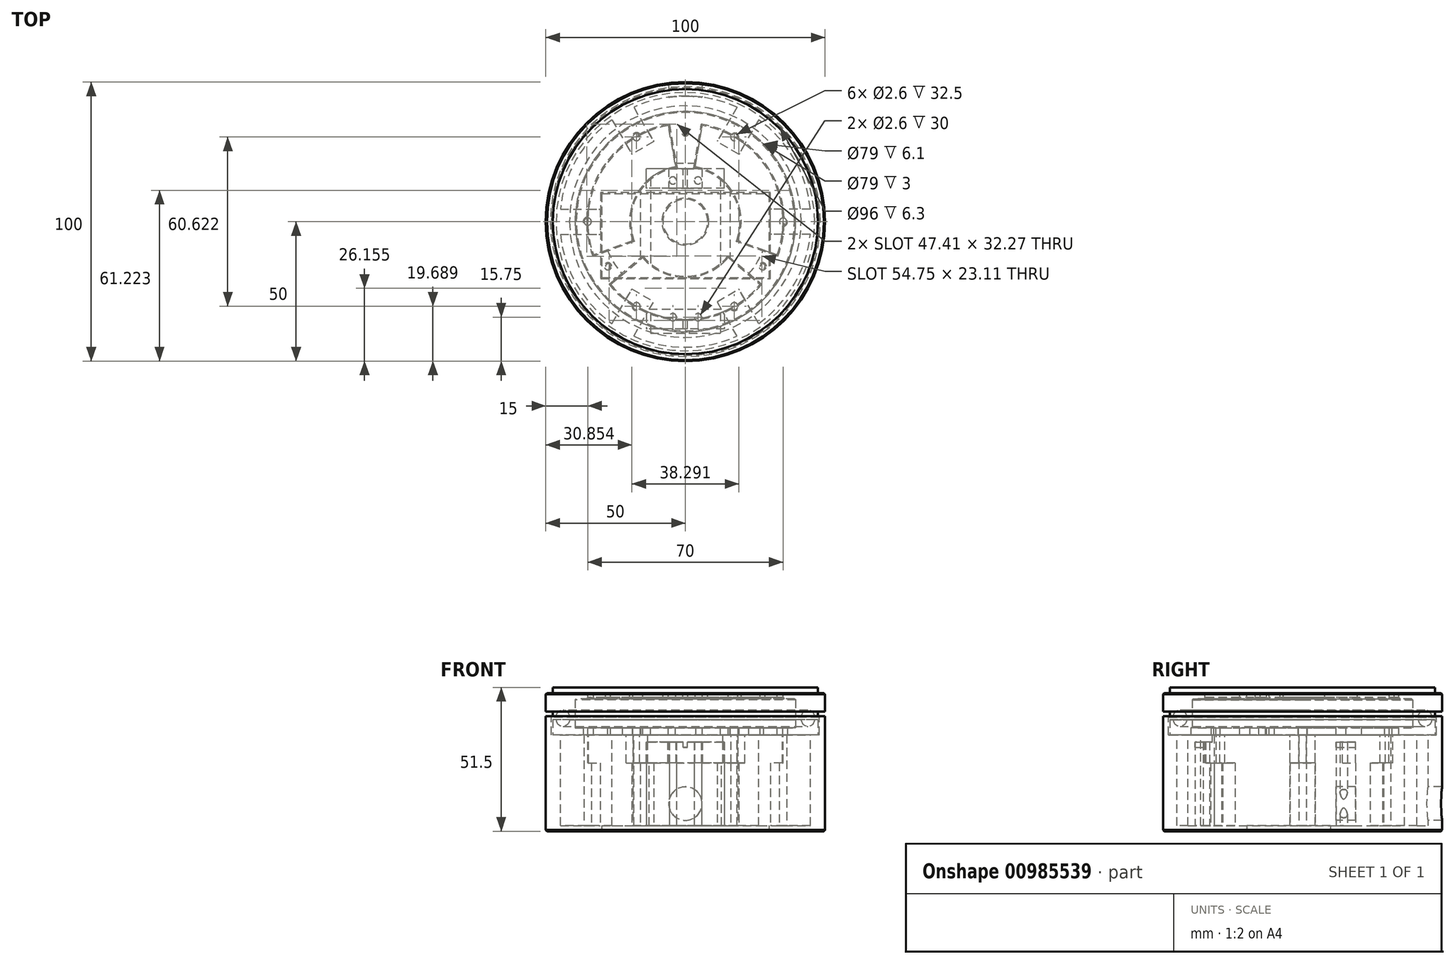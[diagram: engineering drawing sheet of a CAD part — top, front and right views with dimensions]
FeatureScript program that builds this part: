
annotation { "Feature Type Name" : "Feature", "Feature Type Description" : "" }
export const myFeature = defineFeature(function(context is Context, id is Id, definition is map)
    precondition{}
    {
        {
            var Q0;
            Q0=qCreatedBy(makeId("Top.planeOp"),FACE);
            var sketch = newSketch(context, id + "F0", { "sketchPlane" : qUnion([Q0])});
            skCircle(sketch, "E0", {"center": v(0, 0) * mm, "radius": 50 * mm});
            skLineSegment(sketch, "E1.bottom", {"start": v(-30, 10) * mm, "end": v(30, 10) * mm});
            skLineSegment(sketch, "E1.top", {"start": v(-30, -20) * mm, "end": v(30, -20) * mm});
            skLineSegment(sketch, "E1.left", {"start": v(-30, 10) * mm, "end": v(-30, -20) * mm});
            skLineSegment(sketch, "E1.right", {"start": v(30, 10) * mm, "end": v(30, -20) * mm});
            skPoint(sketch, "E2", {"position": v(0, 10) * mm});
            skSolve(sketch);
        }
        {
            var Q0;
            Q0=qSketchRegion(id+"F0",true);
            extrude(context, id + "F1", {"entities" : qUnion([Q0]), "depth" : 2 * mm, "offsetDistance" : 25 * mm});
        }
        {
            var Q0;
            Q0=qCreatedBy(makeId("Front.planeOp"),FACE);
            var sketch = newSketch(context, id + "F2", { "sketchPlane" : qUnion([Q0])});
            skLineSegment(sketch, "E3", {"start": v(45, 2) * mm, "end": v(50, 2) * mm});
            skLineSegment(sketch, "E4", {"start": v(50, 2) * mm, "end": v(50, 41.2) * mm});
            skLineSegment(sketch, "E5", {"start": v(50, 41.2) * mm, "end": v(48, 41.2) * mm});
            skLineSegment(sketch, "E6", {"start": v(48, 41.2) * mm, "end": v(48, 34.5) * mm});
            skLineSegment(sketch, "E7", {"start": v(48, 34.5) * mm, "end": v(45, 34.5) * mm});
            skLineSegment(sketch, "E8", {"start": v(45, 34.5) * mm, "end": v(45, 2) * mm});
            skSolve(sketch);
        }
        {
            var Q0;
            Q0 = qSketchRegion(id + "F2", true);
            var Q1;
            Q1=makeQuery(id+"F1.opExtrude","CAP_EDGE",EDGE,{"disambiguationData":[OSD([sQuery(id+"F0.wireOp",EDGE,"E0")])],"isStart":false});
            sweep(context, id + "F3", {"operationType" : NewBodyOperationType.ADD, "profiles" : qUnion([Q0]), "path" : qUnion([Q1])});
        }
        {
            var Q0;
            {var subQ0=sQuery(id+"F0.wireOp",EDGE,"E0");var subQ1=sQuery(id+"F0.wireOp",EDGE,"wwXRvqXR-i3DQ-b2GX-zRsi-UhwsgNiWwsgo");Q0=makeQuery(id+"F7.boolean.opBoolean","SPLIT",FACE,{"disambiguationData":[TD([makeQuery(id+"F1.opExtrude","SWEPT_FACE",FACE,{"disambiguationData":[OSD([subQ1])]})])],"derivedFrom":makeQuery(id+"F1.opExtrude","CAP_FACE",FACE,{"disambiguationData":[OSD([subQ1,subQ0])],"isStart":false})});}
            var sketch = newSketch(context, id + "F4", { "sketchPlane" : qUnion([Q0])});
            skLineSegment(sketch, "E9.bottom", {"start": v(45.5, -4.5) * mm, "end": v(30.5, -4.5) * mm});
            skLineSegment(sketch, "E9.top", {"start": v(45.5, 4.5) * mm, "end": v(30.5, 4.5) * mm});
            skLineSegment(sketch, "E9.left", {"start": v(45.5, -4.5) * mm, "end": v(45.5, 4.5) * mm});
            skLineSegment(sketch, "E9.right", {"start": v(30.5, -4.5) * mm, "end": v(30.5, 4.5) * mm});
            skPoint(sketch, "E9.middle", {"position": v(38, 0) * mm});
            skCircle(sketch, "E10", {"center": v(35, 0) * mm, "radius": 1.3 * mm});
            skLineSegment(sketch, "E11.1.0", {"start": v(19.15, 24.16) * mm, "end": v(11.35, 28.66) * mm});
            skLineSegment(sketch, "E11.1.1", {"start": v(18.85, 41.65) * mm, "end": v(11.35, 28.66) * mm});
            skCircle(sketch, "E11.1.2", {"center": v(17.5, 30.31) * mm, "radius": 1.3 * mm});
            skLineSegment(sketch, "E11.1.3", {"start": v(26.65, 37.15) * mm, "end": v(18.85, 41.65) * mm});
            skPoint(sketch, "E11.1.4", {"position": v(19, 32.9) * mm});
            skLineSegment(sketch, "E11.1.5", {"start": v(26.65, 37.15) * mm, "end": v(19.15, 24.16) * mm});
            skLineSegment(sketch, "E11.2.0", {"start": v(-11.35, 28.66) * mm, "end": v(-19.15, 24.16) * mm});
            skLineSegment(sketch, "E11.2.1", {"start": v(-26.65, 37.15) * mm, "end": v(-19.15, 24.16) * mm});
            skCircle(sketch, "E11.2.2", {"center": v(-17.5, 30.31) * mm, "radius": 1.3 * mm});
            skLineSegment(sketch, "E11.2.3", {"start": v(-18.85, 41.65) * mm, "end": v(-26.65, 37.15) * mm});
            skPoint(sketch, "E11.2.4", {"position": v(-19, 32.9) * mm});
            skLineSegment(sketch, "E11.2.5", {"start": v(-18.85, 41.65) * mm, "end": v(-11.35, 28.66) * mm});
            skLineSegment(sketch, "E11.3.0", {"start": v(-30.5, 4.5) * mm, "end": v(-30.5, -4.5) * mm});
            skLineSegment(sketch, "E11.3.1", {"start": v(-45.5, -4.5) * mm, "end": v(-30.5, -4.5) * mm});
            skCircle(sketch, "E11.3.2", {"center": v(-35, 0) * mm, "radius": 1.3 * mm});
            skLineSegment(sketch, "E11.3.3", {"start": v(-45.5, 4.5) * mm, "end": v(-45.5, -4.5) * mm});
            skPoint(sketch, "E11.3.4", {"position": v(-38, 0) * mm});
            skLineSegment(sketch, "E11.3.5", {"start": v(-45.5, 4.5) * mm, "end": v(-30.5, 4.5) * mm});
            skLineSegment(sketch, "E11.4.0", {"start": v(-19.15, -24.16) * mm, "end": v(-11.35, -28.66) * mm});
            skLineSegment(sketch, "E11.4.1", {"start": v(-18.85, -41.65) * mm, "end": v(-11.35, -28.66) * mm});
            skCircle(sketch, "E11.4.2", {"center": v(-17.5, -30.31) * mm, "radius": 1.3 * mm});
            skLineSegment(sketch, "E11.4.3", {"start": v(-26.65, -37.15) * mm, "end": v(-18.85, -41.65) * mm});
            skPoint(sketch, "E11.4.4", {"position": v(-19, -32.9) * mm});
            skLineSegment(sketch, "E11.4.5", {"start": v(-26.65, -37.15) * mm, "end": v(-19.15, -24.16) * mm});
            skLineSegment(sketch, "E11.5.0", {"start": v(11.35, -28.66) * mm, "end": v(19.15, -24.16) * mm});
            skLineSegment(sketch, "E11.5.1", {"start": v(26.65, -37.15) * mm, "end": v(19.15, -24.16) * mm});
            skCircle(sketch, "E11.5.2", {"center": v(17.5, -30.31) * mm, "radius": 1.3 * mm});
            skLineSegment(sketch, "E11.5.3", {"start": v(18.85, -41.65) * mm, "end": v(26.65, -37.15) * mm});
            skPoint(sketch, "E11.5.4", {"position": v(19, -32.9) * mm});
            skLineSegment(sketch, "E11.5.5", {"start": v(18.85, -41.65) * mm, "end": v(11.35, -28.66) * mm});
            skPoint(sketch, "E11.center", {"position": v(0, 0) * mm});
            skSolve(sketch);
        }
        {
            var Q0;
            Q0 = qSketchRegion(id + "F4", true);
            var Q1;
            Q1=makeQuery(id+"F3.opSweep","SWEPT_FACE",FACE,{"disambiguationData":[OSD([sQuery(id+"F0.wireOp",EDGE,"E0"),sQuery(id+"F2.wireOp",EDGE,"E7")])]});
            extrude(context, id + "F5", {"entities" : qUnion([Q0]), "operationType" : NewBodyOperationType.ADD, "endBound" : BoundingType.UP_TO_SURFACE, "depth" : 25 * mm, "endBoundEntityFace" : qUnion([Q1]), "offsetDistance" : 25 * mm});
        }
        {
            var Q0;
            Q0=makeQuery(id+"F1.opExtrude","CAP_FACE",FACE,{"disambiguationData":[OSD([sQuery(id+"F0.wireOp",EDGE,"wwXRvqXR-i3DQ-b2GX-zRsi-UhwsgNiWwsgo"),sQuery(id+"F0.wireOp",EDGE,"E0")])],"isStart":false});
            var sketch = newSketch(context, id + "F6", { "sketchPlane" : qUnion([Q0])});
            skLineSegment(sketch, "E12", {"start": v(0, 0) * mm, "end": v(0, 4.6) * mm});
            skCircle(sketch, "E13", {"center": v(-4.5, 14.75) * mm, "radius": 1.3 * mm});
            skLineSegment(sketch, "E14.bottom", {"start": v(14, 12) * mm, "end": v(-14, 12) * mm});
            skLineSegment(sketch, "E14.top", {"start": v(14, 19) * mm, "end": v(-14, 19) * mm});
            skLineSegment(sketch, "E14.left", {"start": v(14, 12) * mm, "end": v(14, 19) * mm});
            skLineSegment(sketch, "E14.right", {"start": v(-14, 12) * mm, "end": v(-14, 19) * mm});
            skPoint(sketch, "E14.middle", {"position": v(0, 15.5) * mm});
            skCircle(sketch, "E15.MirrorC", {"center": v(4.5, 14.75) * mm, "radius": 1.3 * mm});
            skLineSegment(sketch, "E16", {"start": v(13.6, -9.75) * mm, "end": v(-3, -9.75) * mm});
            skPoint(sketch, "E17.MirrorP", {"position": v(0, -35) * mm});
            skLineSegment(sketch, "E18.MirrorCS", {"start": v(-14, -31.5) * mm, "end": v(-14, -38.5) * mm});
            skLineSegment(sketch, "E19.MirrorCS", {"start": v(14, -38.5) * mm, "end": v(-14, -38.5) * mm});
            skLineSegment(sketch, "E20.MirrorCS", {"start": v(14, -31.5) * mm, "end": v(-14, -31.5) * mm});
            skCircle(sketch, "E21.MirrorC", {"center": v(4.5, -34.25) * mm, "radius": 1.3 * mm});
            skLineSegment(sketch, "E22.MirrorCS", {"start": v(14, -31.5) * mm, "end": v(14, -38.5) * mm});
            skCircle(sketch, "E23.MirrorC", {"center": v(-4.5, -34.25) * mm, "radius": 1.3 * mm});
            skSolve(sketch);
        }
        {
            var Q0;
            Q0=qSketchRegion(id+"F6",true);
            extrude(context, id + "F7", {"entities" : qUnion([Q0]), "operationType" : NewBodyOperationType.ADD, "depth" : 30 * mm, "offsetDistance" : 25 * mm});
        }
        {
            var Q0;
            Q0=qCreatedBy(makeId("Front.planeOp"),FACE);
            var sketch = newSketch(context, id + "F8", { "sketchPlane" : qUnion([Q0])});
            skCircle(sketch, "E24", {"center": v(0, 9.9) * mm, "radius": 6 * mm});
            skSolve(sketch);
        }
        {
            var Q0;
            Q0 = qSketchRegion(id + "F8", true);
            extrude(context, id + "F9", {"entities" : qUnion([Q0]), "operationType" : NewBodyOperationType.REMOVE, "oppositeDirection" : true, "depth" : 100 * mm, "offsetDistance" : 25 * mm});
        }
        {
            var Q0;
            Q0=makeQuery(id+"F7.opExtrude","CAP_FACE",FACE,{"disambiguationData":[OSD([sQuery(id+"F6.wireOp",EDGE,"E18.MirrorCS"),sQuery(id+"F6.wireOp",EDGE,"E19.MirrorCS"),sQuery(id+"F6.wireOp",EDGE,"E20.MirrorCS"),sQuery(id+"F6.wireOp",EDGE,"E21.MirrorC"),sQuery(id+"F6.wireOp",EDGE,"E22.MirrorCS"),sQuery(id+"F6.wireOp",EDGE,"E23.MirrorC")])],"isStart":false});
            var sketch = newSketch(context, id + "F10", { "sketchPlane" : qUnion([Q0])});
            skLineSegment(sketch, "E25.bottom", {"start": v(0.75, -39.15) * mm, "end": v(-0.75, -39.15) * mm});
            skLineSegment(sketch, "E25.top", {"start": v(0.75, 20.85) * mm, "end": v(-0.75, 20.85) * mm});
            skLineSegment(sketch, "E25.left", {"start": v(0.75, -39.15) * mm, "end": v(0.75, 20.85) * mm});
            skLineSegment(sketch, "E25.right", {"start": v(-0.75, -39.15) * mm, "end": v(-0.75, 20.85) * mm});
            skPoint(sketch, "E25.middle", {"position": v(0, -9.15) * mm});
            skPoint(sketch, "E25.middle.positionSnap0", {"position": v(0, -31.5) * mm});
            skPoint(sketch, "E25.centerSnap0", {"position": v(0, -31.5) * mm});
            skSolve(sketch);
        }
        {
            var Q0;
            Q0=qSketchRegion(id+"F10",true);
            extrude(context, id + "F11", {"entities" : qUnion([Q0]), "operationType" : NewBodyOperationType.REMOVE, "oppositeDirection" : true, "depth" : 2 * mm, "offsetDistance" : 25 * mm});
        }
        {
            var Q0;
            Q0=makeQuery(id+"F5.boolean.opBoolean","MERGE",FACE,{"derivedFrom":[makeQuery(id+"F3.opSweep","SWEPT_FACE",FACE,{"disambiguationData":[OSD([sQuery(id+"F0.wireOp",EDGE,"E0"),sQuery(id+"F2.wireOp",EDGE,"E7")])]}),makeQuery(id+"F5.opExtrude","CAP_FACE",FACE,{"disambiguationData":[OSD([sQuery(id+"F4.wireOp",EDGE,"Q81txGdN-tRcn-shot-oBIU-nrsWAsqUdM4r.bottom"),sQuery(id+"F4.wireOp",EDGE,"Q81txGdN-tRcn-shot-oBIU-nrsWAsqUdM4r.top"),sQuery(id+"F4.wireOp",EDGE,"Q81txGdN-tRcn-shot-oBIU-nrsWAsqUdM4r.left"),sQuery(id+"F4.wireOp",EDGE,"Q81txGdN-tRcn-shot-oBIU-nrsWAsqUdM4r.right"),sQuery(id+"F4.wireOp",EDGE,"7Wr9KYCT-SgnQ-EfTt-MQro-Hq332cc40vgq")])],"isStart":false}),makeQuery(id+"F5.opExtrude","CAP_FACE",FACE,{"disambiguationData":[OSD([sQuery(id+"F4.wireOp",EDGE,"5effae5a-cc89-4e3e-84d3-61618aa6fbcc.1.0"),sQuery(id+"F4.wireOp",EDGE,"5effae5a-cc89-4e3e-84d3-61618aa6fbcc.1.1"),sQuery(id+"F4.wireOp",EDGE,"5effae5a-cc89-4e3e-84d3-61618aa6fbcc.1.2"),sQuery(id+"F4.wireOp",EDGE,"5effae5a-cc89-4e3e-84d3-61618aa6fbcc.1.3"),sQuery(id+"F4.wireOp",EDGE,"5effae5a-cc89-4e3e-84d3-61618aa6fbcc.1.4")])],"isStart":false}),makeQuery(id+"F5.opExtrude","CAP_FACE",FACE,{"disambiguationData":[OSD([sQuery(id+"F4.wireOp",EDGE,"5effae5a-cc89-4e3e-84d3-61618aa6fbcc.2.0"),sQuery(id+"F4.wireOp",EDGE,"5effae5a-cc89-4e3e-84d3-61618aa6fbcc.2.1"),sQuery(id+"F4.wireOp",EDGE,"5effae5a-cc89-4e3e-84d3-61618aa6fbcc.2.2"),sQuery(id+"F4.wireOp",EDGE,"5effae5a-cc89-4e3e-84d3-61618aa6fbcc.2.3"),sQuery(id+"F4.wireOp",EDGE,"5effae5a-cc89-4e3e-84d3-61618aa6fbcc.2.4")])],"isStart":false}),makeQuery(id+"F5.opExtrude","CAP_FACE",FACE,{"disambiguationData":[OSD([sQuery(id+"F4.wireOp",EDGE,"5effae5a-cc89-4e3e-84d3-61618aa6fbcc.3.0"),sQuery(id+"F4.wireOp",EDGE,"5effae5a-cc89-4e3e-84d3-61618aa6fbcc.3.1"),sQuery(id+"F4.wireOp",EDGE,"5effae5a-cc89-4e3e-84d3-61618aa6fbcc.3.2"),sQuery(id+"F4.wireOp",EDGE,"5effae5a-cc89-4e3e-84d3-61618aa6fbcc.3.3"),sQuery(id+"F4.wireOp",EDGE,"5effae5a-cc89-4e3e-84d3-61618aa6fbcc.3.4")])],"isStart":false}),makeQuery(id+"F5.opExtrude","CAP_FACE",FACE,{"disambiguationData":[OSD([sQuery(id+"F4.wireOp",EDGE,"5c545cf2-7ed1-48a6-9170-971ede2a80a5.2.4.0"),sQuery(id+"F4.wireOp",EDGE,"5c545cf2-7ed1-48a6-9170-971ede2a80a5.3.4.0"),sQuery(id+"F4.wireOp",EDGE,"5c545cf2-7ed1-48a6-9170-971ede2a80a5.5.4.0"),sQuery(id+"F4.wireOp",EDGE,"5c545cf2-7ed1-48a6-9170-971ede2a80a5.8.4.0"),sQuery(id+"F4.wireOp",EDGE,"5c545cf2-7ed1-48a6-9170-971ede2a80a5.11.4.0")])],"isStart":false}),makeQuery(id+"F5.opExtrude","CAP_FACE",FACE,{"disambiguationData":[OSD([sQuery(id+"F4.wireOp",EDGE,"5c545cf2-7ed1-48a6-9170-971ede2a80a5.2.5.0"),sQuery(id+"F4.wireOp",EDGE,"5c545cf2-7ed1-48a6-9170-971ede2a80a5.3.5.0"),sQuery(id+"F4.wireOp",EDGE,"5c545cf2-7ed1-48a6-9170-971ede2a80a5.5.5.0"),sQuery(id+"F4.wireOp",EDGE,"5c545cf2-7ed1-48a6-9170-971ede2a80a5.8.5.0"),sQuery(id+"F4.wireOp",EDGE,"5c545cf2-7ed1-48a6-9170-971ede2a80a5.11.5.0")])],"isStart":false})]});
            var sketch = newSketch(context, id + "F12", { "sketchPlane" : qUnion([Q0])});
            skCircle(sketch, "E26", {"center": v(0, 0) * mm, "radius": 47.5 * mm});
            skCircle(sketch, "E27", {"center": v(35, 0) * mm, "radius": 1.6 * mm});
            skCircle(sketch, "E28.1.0", {"center": v(17.5, 30.31) * mm, "radius": 1.6 * mm});
            skCircle(sketch, "E28.2.0", {"center": v(-17.5, 30.31) * mm, "radius": 1.6 * mm});
            skCircle(sketch, "E28.3.0", {"center": v(-35, 0) * mm, "radius": 1.6 * mm});
            skCircle(sketch, "E28.4.0", {"center": v(-17.5, -30.31) * mm, "radius": 1.6 * mm});
            skCircle(sketch, "E28.5.0", {"center": v(17.5, -30.31) * mm, "radius": 1.6 * mm});
            skLineSegment(sketch, "E29.bottom", {"start": v(-12.5, 21) * mm, "end": v(12.5, 21) * mm});
            skLineSegment(sketch, "E29.top", {"start": v(-12.5, -40) * mm, "end": v(12.5, -40) * mm});
            skLineSegment(sketch, "E29.left", {"start": v(-12.5, 21) * mm, "end": v(-12.5, -40) * mm});
            skLineSegment(sketch, "E29.right", {"start": v(12.5, 21) * mm, "end": v(12.5, -40) * mm});
            skLineSegment(sketch, "E30", {"start": v(16, 0) * mm, "end": v(16, 24.61) * mm});
            skLineSegment(sketch, "E31", {"start": v(16, 0) * mm, "end": v(30, 0) * mm});
            skArc(sketch, "E32", {"start": v(30, 0) * mm, "mid": v(26.05, 14.04) * mm, "end": v(16, 24.61) * mm});
            skLineSegment(sketch, "E33.MirrorCS", {"start": v(16, 0) * mm, "end": v(16, -24.61) * mm});
            skArc(sketch, "E34.MirrorCS", {"start": v(30, 0) * mm, "mid": v(26.05, -14.04) * mm, "end": v(16, -24.61) * mm});
            skArc(sketch, "E35.MirrorCS", {"start": v(-30, 0) * mm, "mid": v(-26.05, 14.04) * mm, "end": v(-16, 24.61) * mm});
            skLineSegment(sketch, "E36.MirrorCS", {"start": v(-16, 0) * mm, "end": v(-30, 0) * mm});
            skArc(sketch, "E37.MirrorCS", {"start": v(-30, 0) * mm, "mid": v(-26.05, -14.04) * mm, "end": v(-16, -24.61) * mm});
            skLineSegment(sketch, "E38.MirrorCS", {"start": v(-16, 0) * mm, "end": v(-16, 24.61) * mm});
            skLineSegment(sketch, "E39.MirrorCS", {"start": v(-16, 0) * mm, "end": v(-16, -24.61) * mm});
            skSolve(sketch);
        }
        {
            var Q0;
            Q0 = qSketchRegion(id + "F12", true);
            extrude(context, id + "F13", {"entities" : qUnion([Q0]), "depth" : 2.5 * mm, "offsetDistance" : 25 * mm});
        }
        {
            var Q0;
            Q0=makeQuery(id+"F13.opExtrude","CAP_FACE",FACE,{"disambiguationData":[OSD([sQuery(id+"F12.wireOp",EDGE,"E26"),sQuery(id+"F12.wireOp",EDGE,"QdyFas2a-h3oe-I2XU-WaBX-7dCjf6wj1iEE"),sQuery(id+"F12.wireOp",EDGE,"E27"),sQuery(id+"F12.wireOp",EDGE,"E28.1.0"),sQuery(id+"F12.wireOp",EDGE,"E28.2.0"),sQuery(id+"F12.wireOp",EDGE,"E28.3.0"),sQuery(id+"F12.wireOp",EDGE,"E28.4.0"),sQuery(id+"F12.wireOp",EDGE,"E28.5.0")])],"isStart":false});
            var sketch = newSketch(context, id + "F14", { "sketchPlane" : qUnion([Q0])});
            skCircle(sketch, "E40", {"center": v(0, 0) * mm, "radius": 47.5 * mm});
            skCircle(sketch, "E41", {"center": v(0, 0) * mm, "radius": 39.5 * mm});
            skSolve(sketch);
        }
        {
            var Q0;
            Q0 = qSketchRegion(id + "F14", true);
            extrude(context, id + "F15", {"entities" : qUnion([Q0]), "operationType" : NewBodyOperationType.ADD, "depth" : 3 * mm, "offsetDistance" : 25 * mm});
        }
        {
            var Q0;
            Q0=qCreatedBy(makeId("Front.planeOp"),FACE);
            var sketch = newSketch(context, id + "F16", { "sketchPlane" : qUnion([Q0])});
            skCircle(sketch, "E42", {"center": v(43.9, 40) * mm, "radius": 2.4 * mm});
            skLineSegment(sketch, "E43", {"start": v(43.9, 40) * mm, "end": v(47.5, 40) * mm});
            skSolve(sketch);
        }
        {
            var Q0;
            Q0 = qSketchRegion(id + "F16", true);
            var Q1;
            Q1=makeQuery(id+"F15.opExtrude","CAP_EDGE",EDGE,{"disambiguationData":[OSD([sQuery(id+"F14.wireOp",EDGE,"E40")])],"isStart":false});
            sweep(context, id + "F17", {"operationType" : NewBodyOperationType.REMOVE, "profiles" : qUnion([Q0]), "path" : qUnion([Q1])});
        }
        {
            var Q0;
            Q0=makeQuery(id+"F3.opSweep","SWEPT_EDGE",EDGE,{"disambiguationData":[OSD([sQuery(id+"F0.wireOp",EDGE,"E0"),sQuery(id+"F2.wireOp",EDGE,"E5"),sQuery(id+"F2.wireOp",EDGE,"E6")])]});
            var Q1;
            Q1=makeQuery(id+"F1.opExtrude","CAP_FACE",FACE,{"disambiguationData":[OSD([sQuery(id+"F0.wireOp",EDGE,"E0"),sQuery(id+"F0.wireOp",EDGE,"E1.bottom"),sQuery(id+"F0.wireOp",EDGE,"E1.top"),sQuery(id+"F0.wireOp",EDGE,"E1.left"),sQuery(id+"F0.wireOp",EDGE,"E1.right")])],"isStart":true});
            chamfer(context, id + "F18", {"entities" : qUnion([Q0, Q1]), "width" : .4 * mm, "tangentPropagation" : true});
        }
        {
            var Q0;
            Q0=makeQuery(id+"F13.opExtrude","CAP_FACE",FACE,{"disambiguationData":[OSD([sQuery(id+"F12.wireOp",EDGE,"E26"),sQuery(id+"F12.wireOp",EDGE,"QdyFas2a-h3oe-I2XU-WaBX-7dCjf6wj1iEE"),sQuery(id+"F12.wireOp",EDGE,"E27"),sQuery(id+"F12.wireOp",EDGE,"E28.1.0"),sQuery(id+"F12.wireOp",EDGE,"E28.2.0"),sQuery(id+"F12.wireOp",EDGE,"E28.3.0"),sQuery(id+"F12.wireOp",EDGE,"E28.4.0"),sQuery(id+"F12.wireOp",EDGE,"E28.5.0")])],"isStart":false});
            cPlane(context, id + "F19", {"entities" : qUnion([Q0]), "cplaneType" : CPlaneType.OFFSET, "offset" : 4 * mm, "width" : 150 * mm, "height" : 150 * mm});
        }
        {
            var Q0;
            Q0=qCreatedBy(id+"F19.planeOp",FACE);
            var sketch = newSketch(context, id + "F20", { "sketchPlane" : qUnion([Q0])});
            skCircle(sketch, "E44", {"center": v(0, 0) * mm, "radius": 47.5 * mm});
            skCircle(sketch, "E45", {"center": v(0, 0) * mm, "radius": 39.5 * mm});
            skSolve(sketch);
        }
        {
            var Q0;
            Q0 = qSketchRegion(id + "F20", true);
            extrude(context, id + "F21", {"entities" : qUnion([Q0]), "depth" : 8.5 * mm, "offsetDistance" : 25 * mm});
        }
        {
            var Q0;
            Q0=qCreatedBy(makeId("Front.planeOp"),FACE);
            var sketch = newSketch(context, id + "F22", { "sketchPlane" : qUnion([Q0])});
            skCircle(sketch, "E46", {"center": v(43.9, 41) * mm, "radius": 2.4 * mm});
            skLineSegment(sketch, "E47", {"start": v(43.9, 41) * mm, "end": v(47.5, 41) * mm});
            skSolve(sketch);
        }
        {
            var Q0;
            Q0 = qSketchRegion(id + "F22", true);
            var Q1;
            Q1=makeQuery(id+"F21.opExtrude","CAP_EDGE",EDGE,{"disambiguationData":[OSD([sQuery(id+"F20.wireOp",EDGE,"E44")])],"isStart":true});
            sweep(context, id + "F23", {"operationType" : NewBodyOperationType.REMOVE, "profiles" : qUnion([Q0]), "path" : qUnion([Q1])});
        }
        {
            var Q0;
            Q0=makeQuery(id+"F21.opExtrude","CAP_FACE",FACE,{"disambiguationData":[OSD([sQuery(id+"F20.wireOp",EDGE,"E44"),sQuery(id+"F20.wireOp",EDGE,"E45")])],"isStart":false});
            var sketch = newSketch(context, id + "F24", { "sketchPlane" : qUnion([Q0])});
            skCircle(sketch, "E48", {"center": v(0, 0) * mm, "radius": 39.5 * mm});
            skCircle(sketch, "E49", {"center": v(0, 0) * mm, "radius": 8 * mm});
            skCircle(sketch, "E50", {"center": v(0, 32) * mm, "radius": 0.9 * mm});
            skCircle(sketch, "E51.1.0", {"center": v(-27.71, 16) * mm, "radius": 0.9 * mm});
            skCircle(sketch, "E51.2.0", {"center": v(-27.71, -16) * mm, "radius": 0.9 * mm});
            skCircle(sketch, "E51.3.0", {"center": v(0, -32) * mm, "radius": 0.9 * mm});
            skCircle(sketch, "E51.4.0", {"center": v(27.71, -16) * mm, "radius": 0.9 * mm});
            skCircle(sketch, "E51.5.0", {"center": v(27.71, 16) * mm, "radius": 0.9 * mm});
            skSolve(sketch);
        }
        {
            var Q0;
            Q0 = qSketchRegion(id + "F24", true);
            extrude(context, id + "F25", {"entities" : qUnion([Q0]), "operationType" : NewBodyOperationType.ADD, "oppositeDirection" : true, "depth" : 2 * mm, "offsetDistance" : 25 * mm});
        }
        {
            var Q0;
            Q0=makeQuery(id+"F25.boolean.opBoolean","MERGE",FACE,{"derivedFrom":[makeQuery(id+"F21.opExtrude","CAP_FACE",FACE,{"disambiguationData":[OSD([sQuery(id+"F20.wireOp",EDGE,"E44"),sQuery(id+"F20.wireOp",EDGE,"E45")])],"isStart":false}),makeQuery(id+"F25.opExtrude","CAP_FACE",FACE,{"disambiguationData":[OSD([sQuery(id+"F24.wireOp",EDGE,"E48"),sQuery(id+"F24.wireOp",EDGE,"yIbnY7o3-wmVO-NjuH-Kyw9-KMAgT1AnqgEH"),sQuery(id+"F24.wireOp",EDGE,"84bf1434-c3ef-48db-a58f-f74dafdd16500.MirrorCS"),sQuery(id+"F24.wireOp",EDGE,"f74ac21c-5909-4822-9f32-811c23cecc18.1.0"),sQuery(id+"F24.wireOp",EDGE,"f74ac21c-5909-4822-9f32-811c23cecc18.1.1"),sQuery(id+"F24.wireOp",EDGE,"f74ac21c-5909-4822-9f32-811c23cecc18.2.0"),sQuery(id+"F24.wireOp",EDGE,"f74ac21c-5909-4822-9f32-811c23cecc18.2.1"),sQuery(id+"F24.wireOp",EDGE,"f74ac21c-5909-4822-9f32-811c23cecc18.3.0"),sQuery(id+"F24.wireOp",EDGE,"f74ac21c-5909-4822-9f32-811c23cecc18.3.1"),sQuery(id+"F24.wireOp",EDGE,"f74ac21c-5909-4822-9f32-811c23cecc18.4.0"),sQuery(id+"F24.wireOp",EDGE,"f74ac21c-5909-4822-9f32-811c23cecc18.4.1"),sQuery(id+"F24.wireOp",EDGE,"f74ac21c-5909-4822-9f32-811c23cecc18.5.0"),sQuery(id+"F24.wireOp",EDGE,"f74ac21c-5909-4822-9f32-811c23cecc18.5.1"),sQuery(id+"F24.wireOp",EDGE,"f74ac21c-5909-4822-9f32-811c23cecc18.6.0"),sQuery(id+"F24.wireOp",EDGE,"f74ac21c-5909-4822-9f32-811c23cecc18.6.1"),sQuery(id+"F24.wireOp",EDGE,"f74ac21c-5909-4822-9f32-811c23cecc18.7.0"),sQuery(id+"F24.wireOp",EDGE,"f74ac21c-5909-4822-9f32-811c23cecc18.7.1"),sQuery(id+"F24.wireOp",EDGE,"f74ac21c-5909-4822-9f32-811c23cecc18.8.0"),sQuery(id+"F24.wireOp",EDGE,"f74ac21c-5909-4822-9f32-811c23cecc18.8.1"),sQuery(id+"F24.wireOp",EDGE,"f74ac21c-5909-4822-9f32-811c23cecc18.9.0"),sQuery(id+"F24.wireOp",EDGE,"f74ac21c-5909-4822-9f32-811c23cecc18.9.1"),sQuery(id+"F24.wireOp",EDGE,"f74ac21c-5909-4822-9f32-811c23cecc18.10.0"),sQuery(id+"F24.wireOp",EDGE,"f74ac21c-5909-4822-9f32-811c23cecc18.10.1"),sQuery(id+"F24.wireOp",EDGE,"f74ac21c-5909-4822-9f32-811c23cecc18.11.0"),sQuery(id+"F24.wireOp",EDGE,"f74ac21c-5909-4822-9f32-811c23cecc18.11.1")])],"isStart":true})]});
            var sketch = newSketch(context, id + "F26", { "sketchPlane" : qUnion([Q0])});
            skCircle(sketch, "E52", {"center": v(0, 0) * mm, "radius": 50 * mm});
            skCircle(sketch, "E53", {"center": v(0, 0) * mm, "radius": 47.5 * mm});
            skSolve(sketch);
        }
        {
            var Q0;
            Q0 = qSketchRegion(id + "F26", true);
            extrude(context, id + "F27", {"entities" : qUnion([Q0]), "operationType" : NewBodyOperationType.ADD, "oppositeDirection" : true, "depth" : 6.6 * mm, "offsetDistance" : 25 * mm});
        }
        {
            var Q0;
            Q0=makeQuery(id+"F27.boolean.opBoolean","MERGE",FACE,{"derivedFrom":[makeQuery(id+"F25.boolean.opBoolean","MERGE",FACE,{"derivedFrom":[makeQuery(id+"F21.opExtrude","CAP_FACE",FACE,{"disambiguationData":[OSD([sQuery(id+"F20.wireOp",EDGE,"E44"),sQuery(id+"F20.wireOp",EDGE,"E45")])],"isStart":false}),makeQuery(id+"F25.opExtrude","CAP_FACE",FACE,{"disambiguationData":[OSD([sQuery(id+"F24.wireOp",EDGE,"E48"),sQuery(id+"F24.wireOp",EDGE,"E49"),sQuery(id+"F24.wireOp",EDGE,"E50"),sQuery(id+"F24.wireOp",EDGE,"E51.1.0"),sQuery(id+"F24.wireOp",EDGE,"E51.2.0"),sQuery(id+"F24.wireOp",EDGE,"E51.3.0"),sQuery(id+"F24.wireOp",EDGE,"E51.4.0"),sQuery(id+"F24.wireOp",EDGE,"E51.5.0")])],"isStart":true})]}),makeQuery(id+"F27.opExtrude","CAP_FACE",FACE,{"disambiguationData":[OSD([sQuery(id+"F26.wireOp",EDGE,"E52"),sQuery(id+"F26.wireOp",EDGE,"E53")])],"isStart":true})]});
            var sketch = newSketch(context, id + "F28", { "sketchPlane" : qUnion([Q0])});
            skArc(sketch, "E54", {"start": v(18.8, -6.84) * mm, "mid": v(17.32, 10) * mm, "end": v(3.47, 19.7) * mm});
            skArc(sketch, "E55", {"start": v(32.89, -11.97) * mm, "mid": v(30.31, 17.5) * mm, "end": v(6.08, 34.47) * mm});
            skLineSegment(sketch, "E56", {"start": v(3.47, 19.7) * mm, "end": v(6.08, 34.47) * mm});
            skLineSegment(sketch, "E57", {"start": v(18.8, -6.84) * mm, "end": v(32.89, -11.97) * mm});
            skLineSegment(sketch, "E58.1.0", {"start": v(-18.8, -6.84) * mm, "end": v(-32.89, -11.97) * mm});
            skArc(sketch, "E58.1.1", {"start": v(-3.47, 19.7) * mm, "mid": v(-17.32, 10) * mm, "end": v(-18.8, -6.84) * mm});
            skArc(sketch, "E58.1.2", {"start": v(-6.08, 34.47) * mm, "mid": v(-30.31, 17.5) * mm, "end": v(-32.89, -11.97) * mm});
            skLineSegment(sketch, "E58.1.3", {"start": v(-3.47, 19.7) * mm, "end": v(-6.08, 34.47) * mm});
            skLineSegment(sketch, "E58.2.0", {"start": v(15.32, -12.86) * mm, "end": v(26.81, -22.5) * mm});
            skArc(sketch, "E58.2.1", {"start": v(-15.32, -12.86) * mm, "mid": v(0, -20) * mm, "end": v(15.32, -12.86) * mm});
            skArc(sketch, "E58.2.2", {"start": v(-26.81, -22.5) * mm, "mid": v(0, -35) * mm, "end": v(26.81, -22.5) * mm});
            skLineSegment(sketch, "E58.2.3", {"start": v(-15.32, -12.86) * mm, "end": v(-26.81, -22.5) * mm});
            skSolve(sketch);
        }
        {
            var Q0;
            Q0 = qSketchRegion(id + "F28", true);
            extrude(context, id + "F29", {"entities" : qUnion([Q0]), "operationType" : NewBodyOperationType.REMOVE, "oppositeDirection" : true, "depth" : 25 * mm, "offsetDistance" : 25 * mm});
        }
        {
            var Q0;
            Q0=makeQuery(id+"F27.boolean.opBoolean","MERGE",FACE,{"derivedFrom":[makeQuery(id+"F25.boolean.opBoolean","MERGE",FACE,{"derivedFrom":[makeQuery(id+"F21.opExtrude","CAP_FACE",FACE,{"disambiguationData":[OSD([sQuery(id+"F20.wireOp",EDGE,"E44"),sQuery(id+"F20.wireOp",EDGE,"E45")])],"isStart":false}),makeQuery(id+"F25.opExtrude","CAP_FACE",FACE,{"disambiguationData":[OSD([sQuery(id+"F24.wireOp",EDGE,"E48"),sQuery(id+"F24.wireOp",EDGE,"3uSXHYaj-E2bH-QVHJ-km1a-R8gfVq9mUm7H"),sQuery(id+"F24.wireOp",EDGE,"5a280829-6924-4c71-9c8d-3301567ad888.1.0"),sQuery(id+"F24.wireOp",EDGE,"5a280829-6924-4c71-9c8d-3301567ad888.2.0"),sQuery(id+"F24.wireOp",EDGE,"5a280829-6924-4c71-9c8d-3301567ad888.3.0"),sQuery(id+"F24.wireOp",EDGE,"5a280829-6924-4c71-9c8d-3301567ad888.4.0"),sQuery(id+"F24.wireOp",EDGE,"5a280829-6924-4c71-9c8d-3301567ad888.5.0"),sQuery(id+"F24.wireOp",EDGE,"E49")])],"isStart":true})]}),makeQuery(id+"F27.opExtrude","CAP_FACE",FACE,{"disambiguationData":[OSD([sQuery(id+"F26.wireOp",EDGE,"E52"),sQuery(id+"F26.wireOp",EDGE,"E53")])],"isStart":true})]});
            var Q1;
            Q1=makeQuery(id+"F25.opExtrude","CAP_FACE",FACE,{"disambiguationData":[OSD([sQuery(id+"F24.wireOp",EDGE,"E48"),sQuery(id+"F24.wireOp",EDGE,"3uSXHYaj-E2bH-QVHJ-km1a-R8gfVq9mUm7H"),sQuery(id+"F24.wireOp",EDGE,"5a280829-6924-4c71-9c8d-3301567ad888.1.0"),sQuery(id+"F24.wireOp",EDGE,"5a280829-6924-4c71-9c8d-3301567ad888.2.0"),sQuery(id+"F24.wireOp",EDGE,"5a280829-6924-4c71-9c8d-3301567ad888.3.0"),sQuery(id+"F24.wireOp",EDGE,"5a280829-6924-4c71-9c8d-3301567ad888.4.0"),sQuery(id+"F24.wireOp",EDGE,"5a280829-6924-4c71-9c8d-3301567ad888.5.0"),sQuery(id+"F24.wireOp",EDGE,"E49")])],"isStart":false});
            chamfer(context, id + "F30", {"entities" : qUnion([Q0, Q1]), "width" : .4 * mm, "tangentPropagation" : true});
        }
        {
            var Q0;
            Q0=makeQuery(id+"F27.boolean.opBoolean","MERGE",FACE,{"derivedFrom":[makeQuery(id+"F25.boolean.opBoolean","MERGE",FACE,{"derivedFrom":[makeQuery(id+"F21.opExtrude","CAP_FACE",FACE,{"disambiguationData":[OSD([sQuery(id+"F20.wireOp",EDGE,"E44"),sQuery(id+"F20.wireOp",EDGE,"E45")])],"isStart":false}),makeQuery(id+"F25.opExtrude","CAP_FACE",FACE,{"disambiguationData":[OSD([sQuery(id+"F24.wireOp",EDGE,"E48"),sQuery(id+"F24.wireOp",EDGE,"3uSXHYaj-E2bH-QVHJ-km1a-R8gfVq9mUm7H"),sQuery(id+"F24.wireOp",EDGE,"5a280829-6924-4c71-9c8d-3301567ad888.1.0"),sQuery(id+"F24.wireOp",EDGE,"5a280829-6924-4c71-9c8d-3301567ad888.2.0"),sQuery(id+"F24.wireOp",EDGE,"5a280829-6924-4c71-9c8d-3301567ad888.3.0"),sQuery(id+"F24.wireOp",EDGE,"5a280829-6924-4c71-9c8d-3301567ad888.4.0"),sQuery(id+"F24.wireOp",EDGE,"5a280829-6924-4c71-9c8d-3301567ad888.5.0"),sQuery(id+"F24.wireOp",EDGE,"E49")])],"isStart":true})]}),makeQuery(id+"F27.opExtrude","CAP_FACE",FACE,{"disambiguationData":[OSD([sQuery(id+"F26.wireOp",EDGE,"E52"),sQuery(id+"F26.wireOp",EDGE,"E53")])],"isStart":true})]});
            var sketch = newSketch(context, id + "F31", { "sketchPlane" : qUnion([Q0])});
            skCircle(sketch, "E59", {"center": v(0, 0) * mm, "radius": 47.5 * mm});
            skSolve(sketch);
        }
        {
            var Q0;
            Q0 = qSketchRegion(id + "F31", true);
            extrude(context, id + "F32", {"entities" : qUnion([Q0]), "depth" : 2 * mm, "offsetDistance" : 25 * mm});
        }
    });
